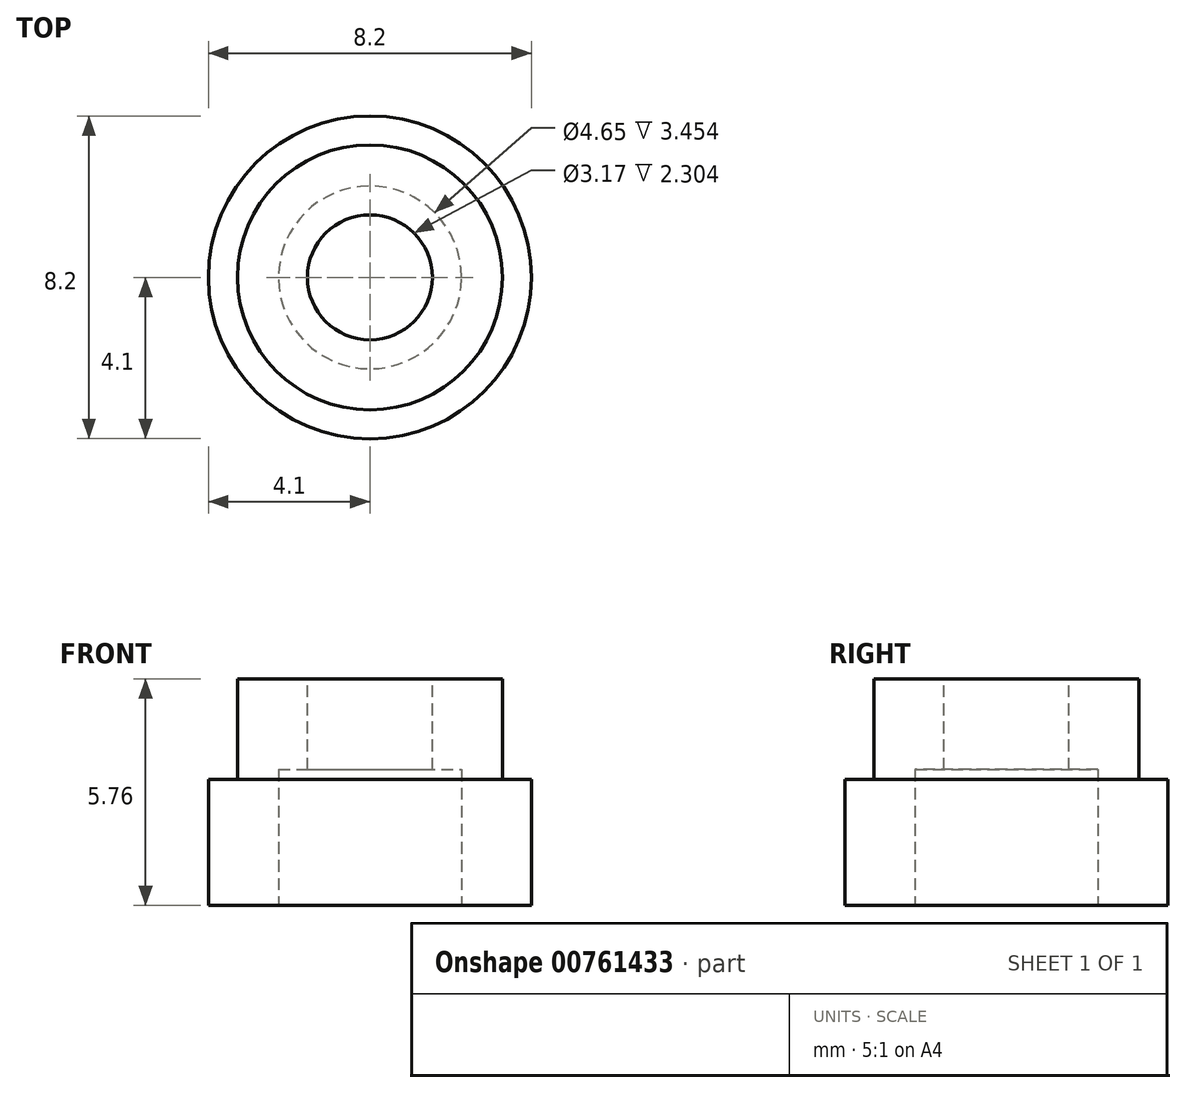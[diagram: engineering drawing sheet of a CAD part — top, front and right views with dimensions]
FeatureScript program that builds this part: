
annotation { "Feature Type Name" : "Feature", "Feature Type Description" : "" }
export const myFeature = defineFeature(function(context is Context, id is Id, definition is map)
    precondition{}
    {
        {
            var Q0;
            Q0=qCreatedBy(makeId("Top.planeOp"),FACE);
            var sketch = newSketch(context, id + "F0", { "sketchPlane" : qUnion([Q0])});
            skCircle(sketch, "E0", {"center": v(0, 0) * mm, "radius": 3.37 * mm});
            skSolve(sketch);
        }
        {
            var Q0;
            Q0 = qSketchRegion(id + "F0", true);
            extrude(context, id + "F1", {"entities" : qUnion([Q0]), "depth" : 2.56 * mm, "offsetDistance" : 25.4 * mm});
        }
        {
            var Q0;
            Q0=makeQuery(id+"F1.opExtrude","CAP_FACE",FACE,{"disambiguationData":[OSD([sQuery(id+"F0.wireOp",EDGE,"E0")])],"isStart":true});
            var sketch = newSketch(context, id + "F2", { "sketchPlane" : qUnion([Q0])});
            skCircle(sketch, "E1", {"center": v(0, 0) * mm, "radius": 4.1 * mm});
            skSolve(sketch);
        }
        {
            var Q0;
            Q0 = qSketchRegion(id + "F2", true);
            extrude(context, id + "F3", {"entities" : qUnion([Q0]), "operationType" : NewBodyOperationType.ADD, "depth" : 3.2 * mm, "offsetDistance" : 25.4 * mm});
        }
        {
            var Q0;
            Q0=makeQuery(id+"F3.opExtrude","CAP_FACE",FACE,{"disambiguationData":[OSD([sQuery(id+"F2.wireOp",EDGE,"E1")])],"isStart":false});
            var sketch = newSketch(context, id + "F4", { "sketchPlane" : qUnion([Q0])});
            skCircle(sketch, "E2", {"center": v(0, 0) * mm, "radius": 2.32 * mm});
            skSolve(sketch);
        }
        {
            var Q0;
            Q0=makeQuery(id+"F4.imprint","IMPRINT",FACE,{"disambiguationData":[TD([[makeQuery(id+"F4.imprint","IMPRINT",EDGE,{"derivedFrom":sQuery(id+"F4.wireOp",EDGE,"E2")}),1.0]])]});
            extrude(context, id + "F5", {"entities" : qUnion([Q0]), "operationType" : NewBodyOperationType.REMOVE, "oppositeDirection" : true, "depth" : 3.45 * mm, "offsetDistance" : 25.4 * mm});
        }
        {
            var Q0;
            Q0=makeQuery(id+"F1.opExtrude","CAP_FACE",FACE,{"disambiguationData":[OSD([sQuery(id+"F0.wireOp",EDGE,"E0")])],"isStart":false});
            var sketch = newSketch(context, id + "F6", { "sketchPlane" : qUnion([Q0])});
            skCircle(sketch, "E3", {"center": v(0, 0) * mm, "radius": 1.59 * mm});
            skSolve(sketch);
        }
        {
            var Q0;
            Q0=makeQuery(id+"F6.imprint","IMPRINT",FACE,{"disambiguationData":[TD([[makeQuery(id+"F6.imprint","IMPRINT",EDGE,{"derivedFrom":sQuery(id+"F6.wireOp",EDGE,"E3")}),1.0]])]});
            extrude(context, id + "F7", {"entities" : qUnion([Q0]), "operationType" : NewBodyOperationType.REMOVE, "oppositeDirection" : true, "depth" : 7.62 * mm, "offsetDistance" : 25.4 * mm});
        }
    });
